# Revit family: IS_Contour21_E5123_BIM_NL
name_source: partatom
category: Plumbing Fixtures
revit_build: Autodesk Revit MEP 2014 (Build: 20130308_1515(x64)
units: mm (PartAtom-declared; Revit-internal decimal feet)

## types (1)
- E512301 - CT21 MIVA WASTAFEL 60CM M.KRG-Z.OVERLOOP
    Accessories = www.idealstandardnederland.nl
    AreaUnits = millimeters
    Assembly Code = C1030200
    AssetType = Vast
    BIMObjectName = ISI_IdealStandard_Wall-HungWashBasins_E512301
    BarCode = 5017830405528
    Brand = Ideal Standard
    CWFU = 0
    CodePerformance = DIN EN 14688 CL 20, DIN EN 31, DIN 18040
    Color = Wit
    ConnectionType = Sanitair
    Cost = 0 $
    Default Elevation = 800 mm  [stored 2.62467 ft]
    Description = Contour 21 / Medical & Care mindervalidenwastafel 600 mm van keramiek. DIN 18024-2/18025-1. 1 kraangat midden doorgestoken. Zonder overloop. Bevestiging met 2 schroeven M10 x 140 mm (K710767). Exclusief bevestigingsmateriaal.
    DrainSize = 0 mm  [stored 0 ft]
    DurationUnit = jaar
    ECA = No
    ExpectedLife = 25
    Features = Mindervalidenwastafel 600 mm van keramiek. DIN 18024-2/18025-1. 1 kraangat midden doorgestoken. Zonder overloop. Bevestiging met 2 schroeven M10 x 140 mm (K710767). Exclusief bevestigingsmateriaal.
    Finish = Wit
    HWFU = 0
    IfcExportAs = IfcSanitaryType
    IfcExportType = WASHHANDBASIN
    InstallationInstructions = http://www.idealstandardnederland.nl
    LinearUnits = millimeters
    ManufacturerURL = www.idealstandardnederland.nl
    Material = Keramiek
    Model = E512301
    ModelNumber = E512301
    ModelReference = Contour 21 / Medical & Care mindervalidenwastafel 600 mm van keramiek. DIN 18024-2/18025-1. 1 kraangat midden doorgestoken. Zonder overloop. Bevestiging met 2 schroeven M10 x 140 mm (K710767). Exclusief bevestigingsmateriaal.
    NBSDescription = Wall hung wash basins
    NBSReference = 45-35-70/369
    Name = Wall-HungWashBasins_E512301_IdealStandard
    NettWeight = 17.598 kg
    NominalDepth = 0 mm  [stored 0 ft]
    NominalHeight = 173 mm
    NominalLength = 553 mm
    NominalWidth = 600 mm
    ProductInformation = http://www.idealstandardnederland.nl
    Shape = Gesculptuurd
    Size = 600 x 553 x 173 mm
    Space = Internal
    URL = www.idealstandardnederland.nl
    Uniclass2015Code = Pr_40_20_96_96
    Uniclass2015Title = Wall-hung wash basins
    Uniclass2015Version = Products v1.1
    Version = 1
    VolumeUnits = liter
    WFU = 0
    WRAS = No
    WarrantyDescription = Fabrieksgarantie
    WarrantyDurationParts = 5
    WarrantyDurationUnit = jaar
    WashHandBasinMounting = Wandhangend
    WashHandBasinType = Mindervalidenwastafel
    WaterEfficientProduct = No

note: [stored X ft] marks values corroborated as IEEE doubles in the binary element streams (Revit-internal decimal feet)

## geometry (parser evidence)
native form markers: Sweep x2
no freeform markers — native parametric forms only
